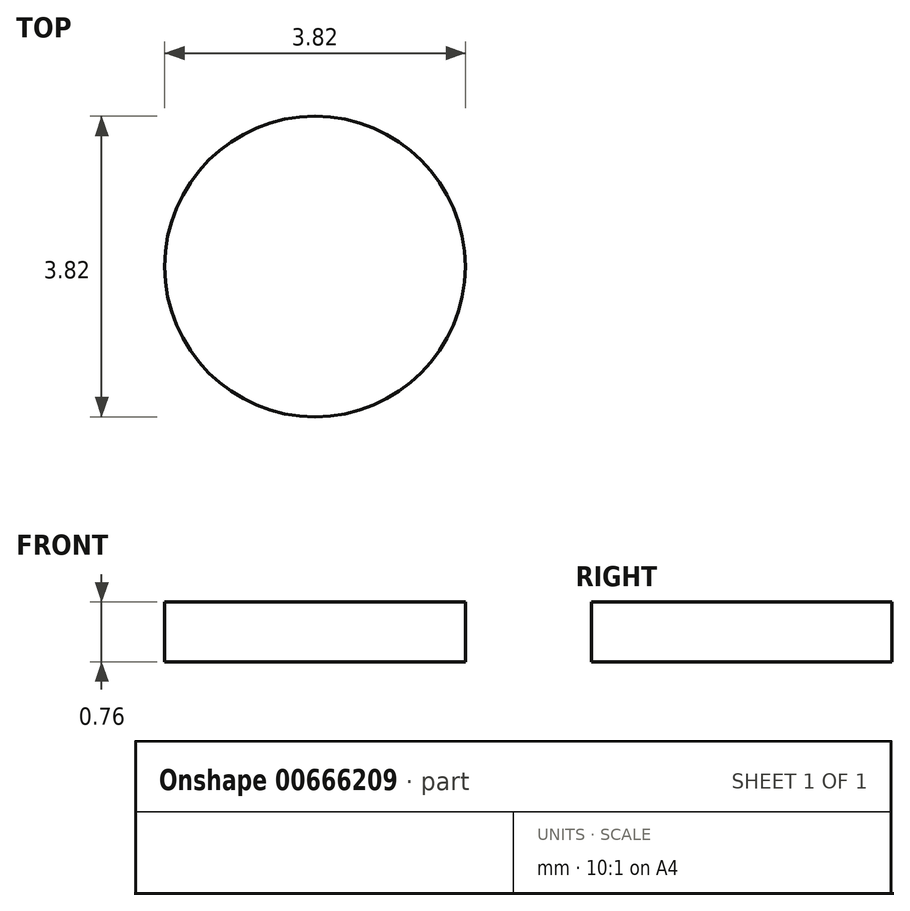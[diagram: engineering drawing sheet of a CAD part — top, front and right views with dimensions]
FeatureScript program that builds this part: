
annotation { "Feature Type Name" : "Feature", "Feature Type Description" : "" }
export const myFeature = defineFeature(function(context is Context, id is Id, definition is map)
    precondition{}
    {
        {
            var Q0;
            Q0=qCreatedBy(makeId("Top.planeOp"),FACE);
            var sketch = newSketch(context, id + "F0", { "sketchPlane" : qUnion([Q0])});
            skLineSegment(sketch, "E0.bottom", {"start": v(-19.6, 3.35) * mm, "end": v(19.6, 3.35) * mm});
            skLineSegment(sketch, "E0.top", {"start": v(-19.6, -3.35) * mm, "end": v(19.6, -3.35) * mm});
            skLineSegment(sketch, "E0.left", {"start": v(-22.07, 0.9) * mm, "end": v(-22.07, -0.9) * mm});
            skLineSegment(sketch, "E0.right", {"start": v(22.07, 0.9) * mm, "end": v(22.07, -0.9) * mm});
            skPoint(sketch, "E0.middle", {"position": v(0, 0) * mm});
            skPoint(sketch, "E1.visualSharp", {"position": v(-22.07, 3.35) * mm});
            skPoint(sketch, "E2.visualSharp", {"position": v(-22.07, -3.35) * mm});
            skArc(sketch, "E3.filletArc", {"start": v(22.07, 0.9) * mm, "mid": v(21.35, 2.63) * mm, "end": v(19.6, 3.35) * mm});
            skArc(sketch, "E4.MirrorCS", {"start": v(22.07, -0.9) * mm, "mid": v(21.35, -2.63) * mm, "end": v(19.6, -3.35) * mm});
            skArc(sketch, "E5.MirrorCS", {"start": v(-22.07, -0.9) * mm, "mid": v(-21.35, -2.63) * mm, "end": v(-19.6, -3.35) * mm});
            skArc(sketch, "E6.MirrorCS", {"start": v(-22.07, 0.9) * mm, "mid": v(-21.35, 2.63) * mm, "end": v(-19.6, 3.35) * mm});
            skSolve(sketch);
        }
        {
            var Q0;
            Q0 = qSketchRegion(id + "F0", true);
            extrude(context, id + "F1", {"entities" : qUnion([Q0]), "depth" : 0.38 * mm, "offsetDistance" : 25.4 * mm, "hasSecondDirection" : true, "secondDirectionOppositeDirection" : true, "secondDirectionDepth" : 0.38 * mm});
        }
        {
            var Q0;
            Q0=makeQuery(id+"F1.opExtrude","CAP_FACE",FACE,{"disambiguationData":[OSD([sQuery(id+"F0.wireOp",EDGE,"E0.bottom"),sQuery(id+"F0.wireOp",EDGE,"E0.top"),sQuery(id+"F0.wireOp",EDGE,"E0.left"),sQuery(id+"F0.wireOp",EDGE,"E0.right"),sQuery(id+"F0.wireOp",EDGE,"E1.filletArc"),sQuery(id+"F0.wireOp",EDGE,"E2.filletArc"),sQuery(id+"F0.wireOp",EDGE,"44869a1e-019a-4017-ada3-4adc95667aa2.filletArc"),sQuery(id+"F0.wireOp",EDGE,"95de6e29-5348-4c54-8bef-5e277698bb9c.filletArc")])],"isStart":false});
            var sketch = newSketch(context, id + "F2", { "sketchPlane" : qUnion([Q0])});
            skCircle(sketch, "E7", {"center": v(19.04, 0) * mm, "radius": 1.9 * mm});
            skCircle(sketch, "E8.MirrorC", {"center": v(-19.04, 0) * mm, "radius": 1.9 * mm});
            skSolve(sketch);
        }
        {
            var Q0;
            Q0=makeQuery(id+"F2.imprint","IMPRINT",FACE,{"disambiguationData":[TD([[makeQuery(id+"F2.imprint","IMPRINT",EDGE,{"derivedFrom":sQuery(id+"F2.wireOp",EDGE,"E8.MirrorC")}),-1.0]])]});
            var Q1;
            Q1=sQuery(id+"F2.wireOp",EDGE,"E8.MirrorC");
            extrude(context, id + "F3", {"entities" : qUnion([Q0]), "operationType" : NewBodyOperationType.REMOVE, "surfaceEntities" : qUnion([Q1]), "oppositeDirection" : true, "depth" : 1.27 * mm, "offsetDistance" : 25.4 * mm, "hasSecondDirection" : true, "secondDirectionOppositeDirection" : false, "secondDirectionDepth" : 0.69 * mm});
        }
        {
            var Q0;
            Q0=makeQuery(id+"F2.imprint","IMPRINT",FACE,{"disambiguationData":[TD([[makeQuery(id+"F2.imprint","IMPRINT",EDGE,{"derivedFrom":sQuery(id+"F2.wireOp",EDGE,"E7")}),1.0]])]});
            var Q1;
            Q1=sQuery(id+"F2.wireOp",EDGE,"E7");
            extrude(context, id + "F4", {"entities" : qUnion([Q0]), "operationType" : NewBodyOperationType.REMOVE, "surfaceEntities" : qUnion([Q1]), "depth" : 0.94 * mm, "offsetDistance" : 25.4 * mm, "hasSecondDirection" : true, "secondDirectionOppositeDirection" : true, "secondDirectionDepth" : 1.8 * mm});
        }
    });
